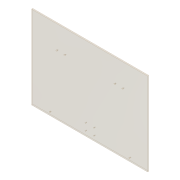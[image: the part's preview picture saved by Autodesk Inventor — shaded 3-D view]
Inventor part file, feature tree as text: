
AUTODESK INVENTOR PART (.ipt)
format: ipt  version: 2012 (Build 160160000, 160)  size: 99,840 bytes
history: native  units: in
note: dims shown in document units (in); Inventor stores cm internally (conversion verified against a paired STEP export)
features: hole x5, pattern_linear x3, extrude x1, sketch x1
ambient origin geometry x8: Origin, YZ Plane, XZ Plane, XY Plane, X Axis, Y Axis, Z Axis, Center Point
bodies: Solid1 (feature_tree)
feature tree (10):
  extrude  "Extrusion1"  Depth=31.5in
  hole  "Hole1"  [1 undecoded]
  pattern_linear  "Rectangular Pattern1"  Count1=2 Spacing1=2.625in
  hole  "Hole2"  [1 undecoded]
  pattern_linear  "Rectangular Pattern2"  Count1=2 Spacing1=3.0in
  hole  "Hole3"  [1 undecoded]
  pattern_linear  "Rectangular Pattern3"  [2 undecoded]
  hole  "Hole4"  [1 undecoded]
  hole  "Hole5"  [1 undecoded]
  sketch  "Sketch1"  dims[d0=44.0in d1=31.5in d2=0.5in d3=0.0in d4=20.4063in d5=1.625in d6=0.265in d7=0.75in d8=0.375in d9=0.25in d10=0.5635in d11=1.0in d12=0.8108in d13=0.7874in d15=2.625in d16=0.7874in d18=3.1875in d19=9.5in d20=8.875in d21=0.265in d22=0.75in d23=0.5in d24=0.25in d25=0.5635in d26=1.0in d27=0.8108in d28=0.7874in d30=3.0in d31=9.5in d32=8.875in d33=0.265in d34=0.75in d35=0.5in d36=0.25in d37=0.5635in d38=1.0in d39=0.8108in d40=0.7874in d42=3.0in d43=1.125in d44=6.875in d45=0.265in d46=0.75in d47=0.5in d48=0.25in d49=0.5635in d50=1.0in d51=0.8108in d52=6.875in d53=1.125in d54=0.265in d55=0.75in d56=0.5in d57=0.25in d58=0.5635in d59=1.0in d60=0.8108in]
note: 7 required parameter values undecoded (feature->parameter linkage not recoverable at this tier; creation-order binding heuristic only, values carry confidence <= 0.55)
